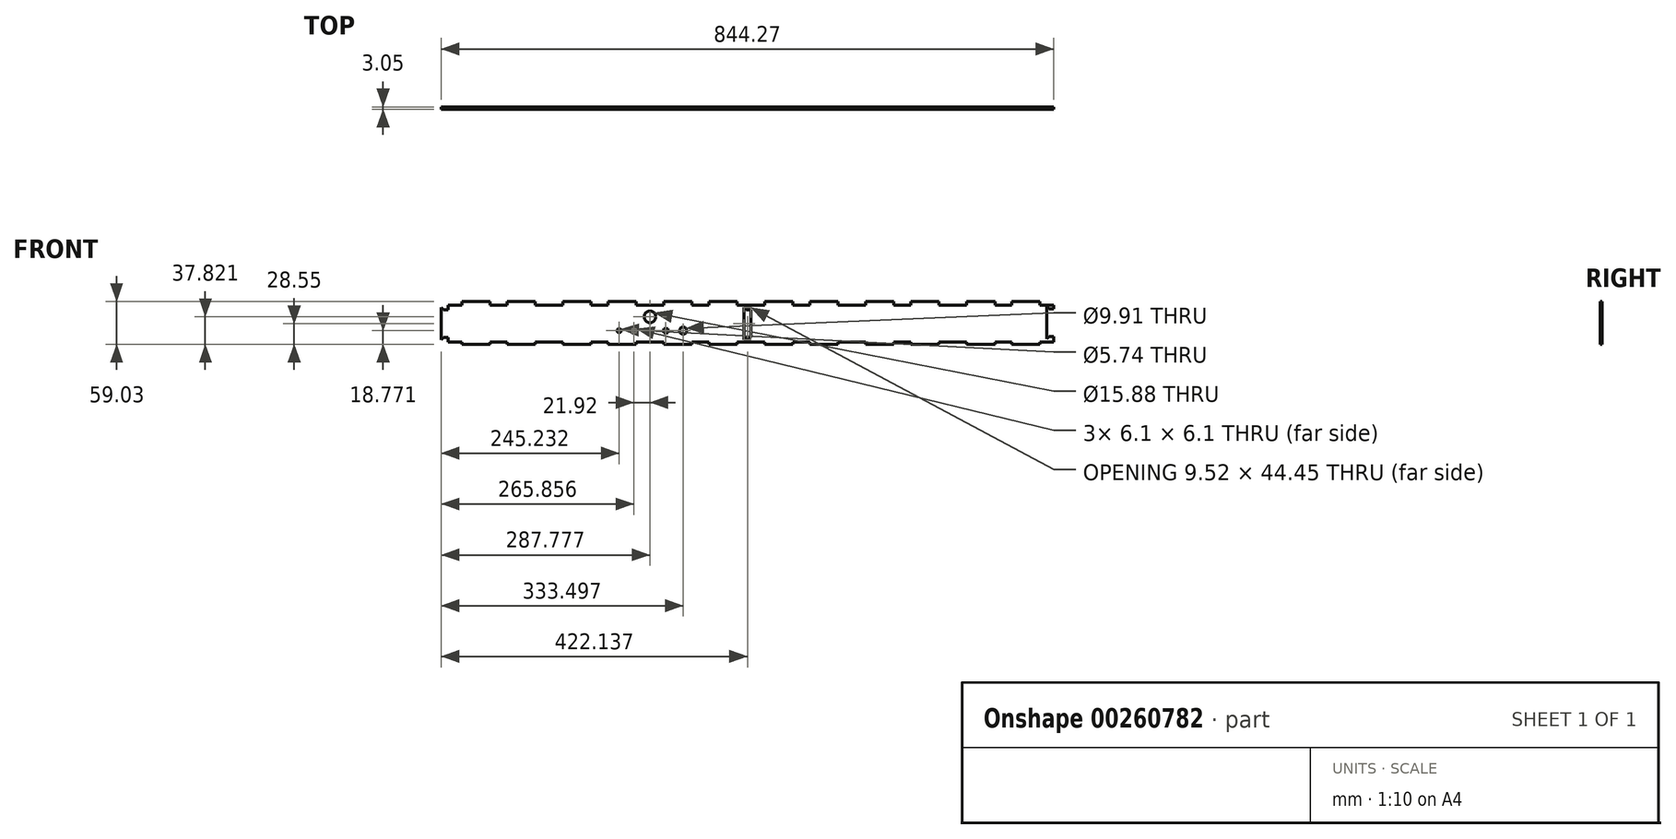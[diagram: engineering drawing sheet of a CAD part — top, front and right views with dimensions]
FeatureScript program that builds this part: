
annotation { "Feature Type Name" : "Feature", "Feature Type Description" : "" }
export const myFeature = defineFeature(function(context is Context, id is Id, definition is map)
    precondition{}
    {
        {
            var Q0;
            Q0=qCreatedBy(makeId("Front.planeOp"),FACE);
            var sketch = newSketch(context, id + "F0", { "sketchPlane" : qUnion([Q0])});
            skLineSegment(sketch, "E0.bottom", {"start": v(0, 0) * mm, "end": v(834.74, 0) * mm});
            skLineSegment(sketch, "E0.top", {"start": v(0, 50.8) * mm, "end": v(834.74, 50.8) * mm});
            skLineSegment(sketch, "E0.left", {"start": v(0, 0) * mm, "end": v(0, 50.8) * mm});
            skLineSegment(sketch, "E0.right", {"start": v(834.74, 0) * mm, "end": v(834.74, 50.8) * mm});
            skLineSegment(sketch, "E1", {"start": v(57.92, 50.8) * mm, "end": v(57.92, 0) * mm, "construction": true});
            skLineSegment(sketch, "E2", {"start": v(75.88, 50.8) * mm, "end": v(75.88, 0) * mm, "construction": true});
            skLineSegment(sketch, "E3", {"start": v(776.82, 50.8) * mm, "end": v(776.82, 0) * mm, "construction": true});
            skLineSegment(sketch, "E4", {"start": v(758.86, 50.8) * mm, "end": v(758.86, 0) * mm, "construction": true});
            skSolve(sketch);
        }
        {
            var Q0;
            Q0=makeQuery(id+"F0.imprint","IMPRINT",FACE,{"disambiguationData":[TD([[makeQuery(id+"F0.imprint","IMPRINT",EDGE,{"derivedFrom":sQuery(id+"F0.wireOp",EDGE,"E0.bottom")}),1.0]])]});
            extrude(context, id + "F1", {"entities" : qUnion([Q0]), "depth" : 3.05 * mm});
        }
        {
            var Q0;
            Q0=makeQuery(id+"F1.opExtrude","CAP_FACE",FACE,{"disambiguationData":[OSD([sQuery(id+"F0.wireOp",EDGE,"E0.bottom"),sQuery(id+"F0.wireOp",EDGE,"E0.top"),sQuery(id+"F0.wireOp",EDGE,"E0.left"),sQuery(id+"F0.wireOp",EDGE,"E0.right")])],"isStart":false});
            var sketch = newSketch(context, id + "F2", { "sketchPlane" : qUnion([Q0])});
            skLineSegment(sketch, "E5", {"start": v(57.92, 0) * mm, "end": v(57.92, 50.8) * mm});
            skLineSegment(sketch, "E6", {"start": v(81.2, 0) * mm, "end": v(81.2, 50.8) * mm});
            skLineSegment(sketch, "E7", {"start": v(776.82, 0) * mm, "end": v(776.82, 50.8) * mm});
            skLineSegment(sketch, "E8", {"start": v(753.54, 0) * mm, "end": v(753.54, 50.8) * mm});
            skLineSegment(sketch, "E9", {"start": v(197.05, 50.8) * mm, "end": v(197.05, 0) * mm});
            skLineSegment(sketch, "E10", {"start": v(220.32, 0) * mm, "end": v(220.32, 50.8) * mm});
            skLineSegment(sketch, "E11", {"start": v(336.17, 50.8) * mm, "end": v(336.17, 0) * mm});
            skLineSegment(sketch, "E12", {"start": v(359.45, 0.94) * mm, "end": v(359.45, 50.8) * mm});
            skLineSegment(sketch, "E13", {"start": v(475.3, 0) * mm, "end": v(475.3, 50.8) * mm});
            skLineSegment(sketch, "E14", {"start": v(498.57, 0) * mm, "end": v(498.57, 50.8) * mm});
            skLineSegment(sketch, "E15", {"start": v(614.42, 50.8) * mm, "end": v(614.42, 0) * mm});
            skLineSegment(sketch, "E16", {"start": v(637.7, 50.8) * mm, "end": v(637.7, 0) * mm});
            skCircle(sketch, "E17", {"center": v(9.53, 25.4) * mm, "radius": 1.27 * mm});
            skPoint(sketch, "E17.centerSnap0", {"position": v(0, 25.4) * mm});
            skCircle(sketch, "E18", {"center": v(825.22, 25.4) * mm, "radius": 1.27 * mm});
            skSolve(sketch);
        }
        {
            var Q0;
            {var subQ0=sQuery(id+"F2.wireOp",EDGE,"E6");Q0=makeQuery(id+"F2.imprint","IMPRINT",FACE,{"disambiguationData":[TD([[makeQuery(id+"F2.imprint","IMPRINT",EDGE,{"derivedFrom":subQ0}),-1.0]])]});}
            var sketch = newSketch(context, id + "F3", { "sketchPlane" : qUnion([Q0])});
            skLineSegment(sketch, "E19", {"start": v(0, 25.4) * mm, "end": v(834.74, 25.4) * mm, "construction": true});
            skLineSegment(sketch, "E20", {"start": v(0, 50.8) * mm, "end": v(0, 55.88) * mm});
            skLineSegment(sketch, "E21", {"start": v(0, 55.88) * mm, "end": v(57.92, 55.88) * mm});
            skLineSegment(sketch, "E22", {"start": v(57.92, 55.88) * mm, "end": v(57.92, 50.8) * mm});
            skLineSegment(sketch, "E23", {"start": v(81.2, 50.8) * mm, "end": v(81.2, 55.88) * mm});
            skLineSegment(sketch, "E24", {"start": v(81.2, 55.88) * mm, "end": v(197.05, 55.88) * mm});
            skLineSegment(sketch, "E25", {"start": v(197.05, 55.88) * mm, "end": v(197.05, 50.8) * mm});
            skLineSegment(sketch, "E26", {"start": v(220.32, 50.8) * mm, "end": v(220.32, 55.88) * mm});
            skLineSegment(sketch, "E27", {"start": v(220.32, 55.88) * mm, "end": v(336.17, 55.88) * mm});
            skLineSegment(sketch, "E28", {"start": v(336.17, 55.88) * mm, "end": v(336.17, 50.8) * mm});
            skLineSegment(sketch, "E29", {"start": v(359.45, 50.8) * mm, "end": v(359.45, 55.88) * mm});
            skLineSegment(sketch, "E30", {"start": v(359.45, 55.88) * mm, "end": v(475.3, 55.88) * mm});
            skLineSegment(sketch, "E31", {"start": v(475.3, 55.88) * mm, "end": v(475.3, 50.8) * mm});
            skLineSegment(sketch, "E32", {"start": v(498.57, 50.8) * mm, "end": v(498.57, 55.88) * mm});
            skLineSegment(sketch, "E33", {"start": v(498.57, 55.88) * mm, "end": v(614.42, 55.88) * mm});
            skLineSegment(sketch, "E34", {"start": v(614.42, 55.88) * mm, "end": v(614.42, 50.8) * mm});
            skLineSegment(sketch, "E35", {"start": v(637.7, 50.8) * mm, "end": v(637.7, 55.88) * mm});
            skLineSegment(sketch, "E36", {"start": v(637.7, 55.88) * mm, "end": v(753.54, 55.88) * mm});
            skLineSegment(sketch, "E37", {"start": v(753.54, 55.88) * mm, "end": v(753.54, 50.8) * mm});
            skLineSegment(sketch, "E38", {"start": v(776.82, 50.8) * mm, "end": v(776.82, 55.88) * mm});
            skLineSegment(sketch, "E39", {"start": v(776.82, 55.88) * mm, "end": v(834.74, 55.88) * mm});
            skLineSegment(sketch, "E40", {"start": v(834.74, 55.88) * mm, "end": v(834.74, 50.8) * mm});
            skLineSegment(sketch, "E41", {"start": v(0, 50.8) * mm, "end": v(834.74, 50.8) * mm});
            skLineSegment(sketch, "E42.bottom", {"start": v(0, 0) * mm, "end": v(57.92, 0) * mm});
            skLineSegment(sketch, "E42.top", {"start": v(0, -3.15) * mm, "end": v(57.92, -3.15) * mm});
            skLineSegment(sketch, "E42.left", {"start": v(0, 0) * mm, "end": v(0, -3.15) * mm});
            skLineSegment(sketch, "E42.right", {"start": v(57.92, 0) * mm, "end": v(57.92, -3.15) * mm});
            skLineSegment(sketch, "E43.bottom", {"start": v(81.2, 0) * mm, "end": v(197.05, 0) * mm});
            skLineSegment(sketch, "E43.top", {"start": v(81.2, -3.15) * mm, "end": v(197.05, -3.15) * mm});
            skLineSegment(sketch, "E43.left", {"start": v(81.2, 0) * mm, "end": v(81.2, -3.15) * mm});
            skLineSegment(sketch, "E43.right", {"start": v(197.05, 0) * mm, "end": v(197.05, -3.15) * mm});
            skLineSegment(sketch, "E44.bottom", {"start": v(220.32, 0) * mm, "end": v(336.17, 0) * mm});
            skLineSegment(sketch, "E44.top", {"start": v(220.32, -3.15) * mm, "end": v(336.17, -3.15) * mm});
            skLineSegment(sketch, "E44.left", {"start": v(220.32, 0) * mm, "end": v(220.32, -3.15) * mm});
            skLineSegment(sketch, "E44.right", {"start": v(336.17, 0) * mm, "end": v(336.17, -3.15) * mm});
            skLineSegment(sketch, "E45.bottom", {"start": v(359.45, 0) * mm, "end": v(475.3, 0) * mm});
            skLineSegment(sketch, "E45.top", {"start": v(359.45, -3.15) * mm, "end": v(475.3, -3.15) * mm});
            skLineSegment(sketch, "E45.left", {"start": v(359.45, 0) * mm, "end": v(359.45, -3.15) * mm});
            skLineSegment(sketch, "E45.right", {"start": v(475.3, 0) * mm, "end": v(475.3, -3.15) * mm});
            skLineSegment(sketch, "E46.bottom", {"start": v(498.57, 0) * mm, "end": v(614.42, 0) * mm});
            skLineSegment(sketch, "E46.top", {"start": v(498.57, -3.15) * mm, "end": v(614.42, -3.15) * mm});
            skLineSegment(sketch, "E46.left", {"start": v(498.57, 0) * mm, "end": v(498.57, -3.15) * mm});
            skLineSegment(sketch, "E46.right", {"start": v(614.42, 0) * mm, "end": v(614.42, -3.15) * mm});
            skLineSegment(sketch, "E47.bottom", {"start": v(637.7, 0) * mm, "end": v(753.54, 0) * mm});
            skLineSegment(sketch, "E47.top", {"start": v(637.7, -3.15) * mm, "end": v(753.54, -3.15) * mm});
            skLineSegment(sketch, "E47.left", {"start": v(637.7, 0) * mm, "end": v(637.7, -3.15) * mm});
            skLineSegment(sketch, "E47.right", {"start": v(753.54, 0) * mm, "end": v(753.54, -3.15) * mm});
            skLineSegment(sketch, "E48.bottom", {"start": v(776.82, 0) * mm, "end": v(834.74, 0) * mm});
            skLineSegment(sketch, "E48.top", {"start": v(776.82, -3.15) * mm, "end": v(834.74, -3.15) * mm});
            skLineSegment(sketch, "E48.left", {"start": v(776.82, 0) * mm, "end": v(776.82, -3.15) * mm});
            skLineSegment(sketch, "E48.right", {"start": v(834.74, 0) * mm, "end": v(834.74, -3.15) * mm});
            skSolve(sketch);
        }
        {
            var Q0;
            {var subQ0=sQuery(id+"F3.wireOp",EDGE,"E20");Q0=makeQuery(id+"F3.imprint","IMPRINT",FACE,{"disambiguationData":[TD([[makeQuery(id+"F3.imprint","IMPRINT",EDGE,{"derivedFrom":subQ0}),-1.0]])]});}
            var Q1;
            {var subQ0=sQuery(id+"F3.wireOp",EDGE,"E23");Q1=makeQuery(id+"F3.imprint","IMPRINT",FACE,{"disambiguationData":[TD([[makeQuery(id+"F3.imprint","IMPRINT",EDGE,{"derivedFrom":subQ0}),-1.0]])]});}
            var Q2;
            {var subQ0=sQuery(id+"F3.wireOp",EDGE,"300d203a-4e24-4113-8f0b-c0bd62af7ee03.MirrorCS");Q2=makeQuery(id+"F3.imprint","IMPRINT",FACE,{"disambiguationData":[TD([[makeQuery(id+"F3.imprint","IMPRINT",EDGE,{"derivedFrom":subQ0}),1.0]])]});}
            var Q3;
            {var subQ0=sQuery(id+"F3.wireOp",EDGE,"300d203a-4e24-4113-8f0b-c0bd62af7ee06.MirrorCS");Q3=makeQuery(id+"F3.imprint","IMPRINT",FACE,{"disambiguationData":[TD([[makeQuery(id+"F3.imprint","IMPRINT",EDGE,{"derivedFrom":subQ0}),1.0]])]});}
            var Q4;
            {var subQ0=sQuery(id+"F3.wireOp",EDGE,"E26");Q4=makeQuery(id+"F3.imprint","IMPRINT",FACE,{"disambiguationData":[TD([[makeQuery(id+"F3.imprint","IMPRINT",EDGE,{"derivedFrom":subQ0}),-1.0]])]});}
            var Q5;
            {var subQ0=sQuery(id+"F3.wireOp",EDGE,"300d203a-4e24-4113-8f0b-c0bd62af7ee09.MirrorCS");Q5=makeQuery(id+"F3.imprint","IMPRINT",FACE,{"disambiguationData":[TD([[makeQuery(id+"F3.imprint","IMPRINT",EDGE,{"derivedFrom":subQ0}),1.0]])]});}
            var Q6;
            {var subQ0=sQuery(id+"F3.wireOp",EDGE,"E29");Q6=makeQuery(id+"F3.imprint","IMPRINT",FACE,{"disambiguationData":[TD([[makeQuery(id+"F3.imprint","IMPRINT",EDGE,{"derivedFrom":subQ0}),-1.0]])]});}
            var Q7;
            {var subQ0=sQuery(id+"F3.wireOp",EDGE,"300d203a-4e24-4113-8f0b-c0bd62af7ee05.MirrorCS");Q7=makeQuery(id+"F3.imprint","IMPRINT",FACE,{"disambiguationData":[TD([[makeQuery(id+"F3.imprint","IMPRINT",EDGE,{"derivedFrom":subQ0}),1.0]])]});}
            var Q8;
            {var subQ0=sQuery(id+"F3.wireOp",EDGE,"E32");Q8=makeQuery(id+"F3.imprint","IMPRINT",FACE,{"disambiguationData":[TD([[makeQuery(id+"F3.imprint","IMPRINT",EDGE,{"derivedFrom":subQ0}),-1.0]])]});}
            var Q9;
            {var subQ0=sQuery(id+"F3.wireOp",EDGE,"300d203a-4e24-4113-8f0b-c0bd62af7ee02.MirrorCS");Q9=makeQuery(id+"F3.imprint","IMPRINT",FACE,{"disambiguationData":[TD([[makeQuery(id+"F3.imprint","IMPRINT",EDGE,{"derivedFrom":subQ0}),1.0]])]});}
            var Q10;
            {var subQ0=sQuery(id+"F3.wireOp",EDGE,"E35");Q10=makeQuery(id+"F3.imprint","IMPRINT",FACE,{"disambiguationData":[TD([[makeQuery(id+"F3.imprint","IMPRINT",EDGE,{"derivedFrom":subQ0}),-1.0]])]});}
            var Q11;
            {var subQ0=sQuery(id+"F3.wireOp",EDGE,"300d203a-4e24-4113-8f0b-c0bd62af7ee00.MirrorCS");Q11=makeQuery(id+"F3.imprint","IMPRINT",FACE,{"disambiguationData":[TD([[makeQuery(id+"F3.imprint","IMPRINT",EDGE,{"derivedFrom":subQ0}),1.0]])]});}
            var Q12;
            {var subQ0=sQuery(id+"F3.wireOp",EDGE,"E38");Q12=makeQuery(id+"F3.imprint","IMPRINT",FACE,{"disambiguationData":[TD([[makeQuery(id+"F3.imprint","IMPRINT",EDGE,{"derivedFrom":subQ0}),-1.0]])]});}
            var Q13;
            {var subQ0=sQuery(id+"F3.wireOp",EDGE,"300d203a-4e24-4113-8f0b-c0bd62af7ee04.MirrorCS");Q13=makeQuery(id+"F3.imprint","IMPRINT",FACE,{"disambiguationData":[TD([[makeQuery(id+"F3.imprint","IMPRINT",EDGE,{"derivedFrom":subQ0}),1.0]])]});}
            var Q14;
            Q14=makeQuery(id+"F3.imprint","IMPRINT",FACE,{"disambiguationData":[TD([[makeQuery(id+"F3.imprint","IMPRINT",EDGE,{"derivedFrom":sQuery(id+"F3.wireOp",EDGE,"E42.bottom")}),-1.0]])]});
            var Q15;
            Q15=makeQuery(id+"F3.imprint","IMPRINT",FACE,{"disambiguationData":[TD([[makeQuery(id+"F3.imprint","IMPRINT",EDGE,{"derivedFrom":sQuery(id+"F3.wireOp",EDGE,"E43.bottom")}),-1.0]])]});
            var Q16;
            Q16=makeQuery(id+"F3.imprint","IMPRINT",FACE,{"disambiguationData":[TD([[makeQuery(id+"F3.imprint","IMPRINT",EDGE,{"derivedFrom":sQuery(id+"F3.wireOp",EDGE,"E44.bottom")}),-1.0]])]});
            var Q17;
            Q17=makeQuery(id+"F3.imprint","IMPRINT",FACE,{"disambiguationData":[TD([[makeQuery(id+"F3.imprint","IMPRINT",EDGE,{"derivedFrom":sQuery(id+"F3.wireOp",EDGE,"E45.bottom")}),-1.0]])]});
            var Q18;
            Q18=makeQuery(id+"F3.imprint","IMPRINT",FACE,{"disambiguationData":[TD([[makeQuery(id+"F3.imprint","IMPRINT",EDGE,{"derivedFrom":sQuery(id+"F3.wireOp",EDGE,"E46.bottom")}),-1.0]])]});
            var Q19;
            Q19=makeQuery(id+"F3.imprint","IMPRINT",FACE,{"disambiguationData":[TD([[makeQuery(id+"F3.imprint","IMPRINT",EDGE,{"derivedFrom":sQuery(id+"F3.wireOp",EDGE,"E47.bottom")}),-1.0]])]});
            var Q20;
            Q20=makeQuery(id+"F3.imprint","IMPRINT",FACE,{"disambiguationData":[TD([[makeQuery(id+"F3.imprint","IMPRINT",EDGE,{"derivedFrom":sQuery(id+"F3.wireOp",EDGE,"E48.bottom")}),-1.0]])]});
            extrude(context, id + "F4", {"entities" : qUnion([Q0, Q1, Q2, Q3, Q4, Q5, Q6, Q7, Q8, Q9, Q10, Q11, Q12, Q13, Q14, Q15, Q16, Q17, Q18, Q19, Q20]), "operationType" : NewBodyOperationType.ADD, "oppositeDirection" : true, "depth" : 3.05 * mm});
        }
        {
            var Q0;
            {var subQ0=sQuery(id+"F2.wireOp",EDGE,"E6");Q0=makeQuery(id+"F2.imprint","IMPRINT",FACE,{"disambiguationData":[TD([[makeQuery(id+"F2.imprint","IMPRINT",EDGE,{"derivedFrom":subQ0}),-1.0]])]});}
            var sketch = newSketch(context, id + "F5", { "sketchPlane" : qUnion([Q0])});
            skLineSegment(sketch, "E49", {"start": v(0, 6.35) * mm, "end": v(0, 44.45) * mm});
            skPoint(sketch, "E50", {"position": v(0, 25.4) * mm});
            skLineSegment(sketch, "E51", {"start": v(0, 44.45) * mm, "end": v(-6.35, 44.45) * mm});
            skLineSegment(sketch, "E52", {"start": v(0, 6.35) * mm, "end": v(-6.35, 6.35) * mm});
            skLineSegment(sketch, "E53", {"start": v(-6.35, 44.45) * mm, "end": v(-9.52, 47.63) * mm});
            skLineSegment(sketch, "E54", {"start": v(-6.35, 6.35) * mm, "end": v(-9.52, 3.18) * mm});
            skLineSegment(sketch, "E55", {"start": v(-9.52, 47.63) * mm, "end": v(-9.52, 3.18) * mm});
            skLineSegment(sketch, "E56", {"start": v(834.74, 7.32) * mm, "end": v(834.74, 45.42) * mm});
            skPoint(sketch, "E57", {"position": v(834.74, 26.37) * mm});
            skLineSegment(sketch, "E58", {"start": v(834.74, 45.42) * mm, "end": v(828.4, 45.42) * mm});
            skLineSegment(sketch, "E59", {"start": v(834.74, 7.32) * mm, "end": v(828.4, 7.32) * mm});
            skLineSegment(sketch, "E60", {"start": v(828.4, 45.42) * mm, "end": v(825.22, 48.6) * mm});
            skLineSegment(sketch, "E61", {"start": v(828.4, 7.32) * mm, "end": v(825.22, 4.14) * mm});
            skLineSegment(sketch, "E62", {"start": v(825.22, 48.6) * mm, "end": v(825.22, 4.14) * mm});
            skSolve(sketch);
        }
        {
            var Q0;
            Q0=makeQuery(id+"F5.imprint","IMPRINT",FACE,{"disambiguationData":[TD([[makeQuery(id+"F5.imprint","IMPRINT",EDGE,{"derivedFrom":sQuery(id+"F5.wireOp",EDGE,"E49")}),1.0]])]});
            extrude(context, id + "F6", {"entities" : qUnion([Q0]), "operationType" : NewBodyOperationType.ADD, "oppositeDirection" : true, "depth" : 3.05 * mm});
        }
        {
            var Q0;
            Q0=makeQuery(id+"F5.imprint","IMPRINT",FACE,{"disambiguationData":[TD([[makeQuery(id+"F5.imprint","IMPRINT",EDGE,{"derivedFrom":sQuery(id+"F5.wireOp",EDGE,"E56")}),1.0]])]});
            extrude(context, id + "F7", {"entities" : qUnion([Q0]), "operationType" : NewBodyOperationType.REMOVE, "endBound" : BoundingType.THROUGH_ALL, "oppositeDirection" : true, "depth" : 25.4 * mm});
        }
        {
            var Q0;
            {var subQ0=sQuery(id+"F2.wireOp",EDGE,"E11");Q0=makeQuery(id+"F2.imprint","IMPRINT",FACE,{"disambiguationData":[TD([[makeQuery(id+"F2.imprint","IMPRINT",EDGE,{"derivedFrom":subQ0}),1.0]])]});}
            var sketch = newSketch(context, id + "F8", { "sketchPlane" : qUnion([Q0])});
            skLineSegment(sketch, "E63", {"start": v(417.37, 6.35) * mm, "end": v(417.37, 44.45) * mm});
            skLineSegment(sketch, "E64", {"start": v(417.37, 44.45) * mm, "end": v(411.02, 44.45) * mm});
            skLineSegment(sketch, "E65", {"start": v(411.02, 44.45) * mm, "end": v(407.85, 47.63) * mm});
            skLineSegment(sketch, "E66", {"start": v(407.85, 47.63) * mm, "end": v(407.85, 3.18) * mm});
            skLineSegment(sketch, "E67", {"start": v(407.85, 3.17) * mm, "end": v(411.02, 6.35) * mm});
            skLineSegment(sketch, "E68", {"start": v(411.02, 6.35) * mm, "end": v(417.37, 6.35) * mm});
            skPoint(sketch, "E69", {"position": v(417.37, 25.4) * mm});
            skPoint(sketch, "E70", {"position": v(407.85, 25.4) * mm});
            skLineSegment(sketch, "E71", {"start": v(407.85, 25.4) * mm, "end": v(417.37, 25.4) * mm, "construction": true});
            skSolve(sketch);
        }
        {
            var Q0;
            {var subQ0=sQuery(id+"F2.wireOp",EDGE,"E10");Q0=makeQuery(id+"F2.imprint","IMPRINT",FACE,{"disambiguationData":[TD([[makeQuery(id+"F2.imprint","IMPRINT",EDGE,{"derivedFrom":subQ0}),-1.0]])]});}
            var sketch = newSketch(context, id + "F9", { "sketchPlane" : qUnion([Q0])});
            skLineSegment(sketch, "E72.bottom", {"start": v(245.23, 21.59) * mm, "end": v(311.27, 21.59) * mm, "construction": true});
            skLineSegment(sketch, "E72.top", {"start": v(245.23, 9.65) * mm, "end": v(311.27, 9.65) * mm, "construction": true});
            skLineSegment(sketch, "E72.left", {"start": v(245.23, 21.59) * mm, "end": v(245.23, 9.65) * mm, "construction": true});
            skLineSegment(sketch, "E72.right", {"start": v(311.27, 21.59) * mm, "end": v(311.27, 9.65) * mm, "construction": true});
            skPoint(sketch, "E73", {"position": v(278.25, 9.65) * mm});
            skLineSegment(sketch, "E74.bottom", {"start": v(253.28, 12.57) * mm, "end": v(259.37, 12.57) * mm});
            skLineSegment(sketch, "E74.top", {"start": v(253.28, 18.67) * mm, "end": v(259.37, 18.67) * mm});
            skLineSegment(sketch, "E74.left", {"start": v(253.28, 12.57) * mm, "end": v(253.28, 18.67) * mm});
            skLineSegment(sketch, "E74.right", {"start": v(259.37, 12.57) * mm, "end": v(259.37, 18.67) * mm});
            skLineSegment(sketch, "E75.bottom", {"start": v(275.2, 12.57) * mm, "end": v(281.3, 12.57) * mm});
            skLineSegment(sketch, "E75.top", {"start": v(275.2, 18.67) * mm, "end": v(281.3, 18.67) * mm});
            skLineSegment(sketch, "E75.left", {"start": v(275.2, 12.57) * mm, "end": v(275.2, 18.67) * mm});
            skLineSegment(sketch, "E75.right", {"start": v(281.3, 12.57) * mm, "end": v(281.3, 18.67) * mm});
            skLineSegment(sketch, "E76.bottom", {"start": v(297.12, 12.57) * mm, "end": v(303.21, 12.57) * mm});
            skLineSegment(sketch, "E76.top", {"start": v(297.12, 18.67) * mm, "end": v(303.21, 18.67) * mm});
            skLineSegment(sketch, "E76.left", {"start": v(297.12, 12.57) * mm, "end": v(297.12, 18.67) * mm});
            skLineSegment(sketch, "E76.right", {"start": v(303.21, 12.57) * mm, "end": v(303.21, 18.67) * mm});
            skPoint(sketch, "E77", {"position": v(253.28, 15.62) * mm});
            skPoint(sketch, "E78", {"position": v(245.23, 15.62) * mm});
            skPoint(sketch, "E79", {"position": v(278.25, 18.67) * mm});
            skPoint(sketch, "E80", {"position": v(275.2, 15.62) * mm});
            skPoint(sketch, "E81", {"position": v(297.12, 15.62) * mm});
            skPoint(sketch, "E82", {"position": v(300.17, 18.67) * mm});
            skCircle(sketch, "E83", {"center": v(235.7, 15.62) * mm, "radius": 2.87 * mm});
            skCircle(sketch, "E84", {"center": v(323.97, 15.62) * mm, "radius": 4.95 * mm});
            skCircle(sketch, "E85", {"center": v(278.25, 34.67) * mm, "radius": 7.94 * mm});
            skSolve(sketch);
        }
        {
            var Q0;
            Q0=qSketchRegion(id+"F9",true);
            extrude(context, id + "F10", {"entities" : qUnion([Q0]), "operationType" : NewBodyOperationType.REMOVE, "endBound" : BoundingType.THROUGH_ALL, "oppositeDirection" : true, "depth" : 25.4 * mm});
        }
        {
            var Q0;
            Q0=qSketchRegion(id+"F8",true);
            extrude(context, id + "F11", {"entities" : qUnion([Q0]), "operationType" : NewBodyOperationType.REMOVE, "oppositeDirection" : true, "depth" : 25.4 * mm});
        }
        {
            var Q0;
            {var subQ0=sQuery(id+"F2.wireOp",EDGE,"E6");Q0=makeQuery(id+"F2.imprint","IMPRINT",FACE,{"disambiguationData":[TD([[makeQuery(id+"F2.imprint","IMPRINT",EDGE,{"derivedFrom":subQ0}),-1.0]])]});}
            var sketch = newSketch(context, id + "F12", { "sketchPlane" : qUnion([Q0])});
            skLineSegment(sketch, "E86.bottom", {"start": v(120.07, 55.88) * mm, "end": v(158.17, 55.88) * mm});
            skLineSegment(sketch, "E86.top", {"start": v(120.07, 50.8) * mm, "end": v(158.17, 50.8) * mm});
            skLineSegment(sketch, "E86.left", {"start": v(120.07, 55.88) * mm, "end": v(120.07, 50.8) * mm});
            skLineSegment(sketch, "E86.right", {"start": v(158.17, 55.88) * mm, "end": v(158.17, 50.8) * mm});
            skLineSegment(sketch, "E87.bottom", {"start": v(259.2, 55.88) * mm, "end": v(297.3, 55.88) * mm});
            skLineSegment(sketch, "E87.top", {"start": v(259.2, 50.8) * mm, "end": v(297.3, 50.8) * mm});
            skLineSegment(sketch, "E87.left", {"start": v(259.2, 55.88) * mm, "end": v(259.2, 50.8) * mm});
            skLineSegment(sketch, "E87.right", {"start": v(297.3, 55.88) * mm, "end": v(297.3, 50.8) * mm});
            skLineSegment(sketch, "E88.bottom", {"start": v(398.32, 55.88) * mm, "end": v(436.42, 55.88) * mm});
            skLineSegment(sketch, "E88.top", {"start": v(398.32, 50.8) * mm, "end": v(436.42, 50.8) * mm});
            skLineSegment(sketch, "E88.left", {"start": v(398.32, 55.88) * mm, "end": v(398.32, 50.8) * mm});
            skLineSegment(sketch, "E88.right", {"start": v(436.42, 55.88) * mm, "end": v(436.42, 50.8) * mm});
            skLineSegment(sketch, "E89.bottom", {"start": v(537.44, 55.88) * mm, "end": v(575.54, 55.88) * mm});
            skLineSegment(sketch, "E89.top", {"start": v(537.44, 50.8) * mm, "end": v(575.54, 50.8) * mm});
            skLineSegment(sketch, "E89.left", {"start": v(537.44, 55.88) * mm, "end": v(537.44, 50.8) * mm});
            skLineSegment(sketch, "E89.right", {"start": v(575.54, 55.88) * mm, "end": v(575.54, 50.8) * mm});
            skLineSegment(sketch, "E90.bottom", {"start": v(676.57, 55.88) * mm, "end": v(714.67, 55.88) * mm});
            skLineSegment(sketch, "E90.top", {"start": v(676.57, 50.8) * mm, "end": v(714.67, 50.8) * mm});
            skLineSegment(sketch, "E90.left", {"start": v(676.57, 55.88) * mm, "end": v(676.57, 50.8) * mm});
            skLineSegment(sketch, "E90.right", {"start": v(714.67, 55.88) * mm, "end": v(714.67, 50.8) * mm});
            skLineSegment(sketch, "E91.bottom", {"start": v(815.7, 55.88) * mm, "end": v(853.8, 55.88) * mm});
            skLineSegment(sketch, "E91.top", {"start": v(815.7, 50.8) * mm, "end": v(853.8, 50.8) * mm});
            skLineSegment(sketch, "E91.left", {"start": v(815.7, 55.88) * mm, "end": v(815.7, 50.8) * mm});
            skLineSegment(sketch, "E91.right", {"start": v(853.8, 55.88) * mm, "end": v(853.8, 50.8) * mm});
            skLineSegment(sketch, "E92.bottom", {"start": v(19.05, 50.8) * mm, "end": v(-19.05, 50.8) * mm});
            skLineSegment(sketch, "E92.top", {"start": v(19.05, 55.88) * mm, "end": v(-19.05, 55.88) * mm});
            skLineSegment(sketch, "E92.left", {"start": v(19.05, 50.8) * mm, "end": v(19.05, 55.88) * mm});
            skLineSegment(sketch, "E92.right", {"start": v(-19.05, 50.8) * mm, "end": v(-19.05, 55.88) * mm});
            skLineSegment(sketch, "E93.bottom", {"start": v(19.05, -3.15) * mm, "end": v(-19.05, -3.15) * mm});
            skLineSegment(sketch, "E93.top", {"start": v(19.05, 0) * mm, "end": v(-19.05, 0) * mm});
            skLineSegment(sketch, "E93.left", {"start": v(19.05, -3.15) * mm, "end": v(19.05, 0) * mm});
            skLineSegment(sketch, "E93.right", {"start": v(-19.05, -3.15) * mm, "end": v(-19.05, 0) * mm});
            skLineSegment(sketch, "E94.bottom", {"start": v(158.17, -3.15) * mm, "end": v(120.07, -3.15) * mm});
            skLineSegment(sketch, "E94.top", {"start": v(158.17, 0) * mm, "end": v(120.07, 0) * mm});
            skLineSegment(sketch, "E94.left", {"start": v(158.17, -3.15) * mm, "end": v(158.17, 0) * mm});
            skLineSegment(sketch, "E94.right", {"start": v(120.07, -3.15) * mm, "end": v(120.07, 0) * mm});
            skLineSegment(sketch, "E95.bottom", {"start": v(297.3, -3.15) * mm, "end": v(259.2, -3.15) * mm});
            skLineSegment(sketch, "E95.top", {"start": v(297.3, 0) * mm, "end": v(259.2, 0) * mm});
            skLineSegment(sketch, "E95.left", {"start": v(297.3, -3.15) * mm, "end": v(297.3, 0) * mm});
            skLineSegment(sketch, "E95.right", {"start": v(259.2, -3.15) * mm, "end": v(259.2, 0) * mm});
            skLineSegment(sketch, "E96.bottom", {"start": v(436.42, -3.15) * mm, "end": v(398.32, -3.15) * mm});
            skLineSegment(sketch, "E96.top", {"start": v(436.42, 0) * mm, "end": v(398.32, 0) * mm});
            skLineSegment(sketch, "E96.left", {"start": v(436.42, -3.15) * mm, "end": v(436.42, 0) * mm});
            skLineSegment(sketch, "E96.right", {"start": v(398.32, -3.15) * mm, "end": v(398.32, 0) * mm});
            skLineSegment(sketch, "E97.bottom", {"start": v(575.54, -3.15) * mm, "end": v(537.44, -3.15) * mm});
            skLineSegment(sketch, "E97.top", {"start": v(575.54, 0) * mm, "end": v(537.44, 0) * mm});
            skLineSegment(sketch, "E97.left", {"start": v(575.54, -3.15) * mm, "end": v(575.54, 0) * mm});
            skLineSegment(sketch, "E97.right", {"start": v(537.44, -3.15) * mm, "end": v(537.44, 0) * mm});
            skLineSegment(sketch, "E98.bottom", {"start": v(714.67, -3.15) * mm, "end": v(676.57, -3.15) * mm});
            skLineSegment(sketch, "E98.top", {"start": v(714.67, 0) * mm, "end": v(676.57, 0) * mm});
            skLineSegment(sketch, "E98.left", {"start": v(714.67, -3.15) * mm, "end": v(714.67, 0) * mm});
            skLineSegment(sketch, "E98.right", {"start": v(676.57, -3.15) * mm, "end": v(676.57, 0) * mm});
            skLineSegment(sketch, "E99.bottom", {"start": v(853.8, -3.15) * mm, "end": v(815.7, -3.15) * mm});
            skLineSegment(sketch, "E99.top", {"start": v(853.8, 0) * mm, "end": v(815.7, 0) * mm});
            skLineSegment(sketch, "E99.left", {"start": v(853.8, -3.15) * mm, "end": v(853.8, 0) * mm});
            skLineSegment(sketch, "E99.right", {"start": v(815.7, -3.15) * mm, "end": v(815.7, 0) * mm});
            skPoint(sketch, "E100", {"position": v(0, 55.88) * mm});
            skPoint(sketch, "E101", {"position": v(139.12, 55.88) * mm});
            skPoint(sketch, "E102", {"position": v(278.25, 55.88) * mm});
            skPoint(sketch, "E103", {"position": v(417.37, 55.88) * mm});
            skPoint(sketch, "E104", {"position": v(556.5, 55.88) * mm});
            skPoint(sketch, "E105", {"position": v(695.62, 55.88) * mm});
            skPoint(sketch, "E106", {"position": v(834.74, 55.88) * mm});
            skPoint(sketch, "E107", {"position": v(834.74, -3.15) * mm});
            skPoint(sketch, "E108", {"position": v(695.62, -3.15) * mm});
            skPoint(sketch, "E109", {"position": v(556.5, -3.15) * mm});
            skPoint(sketch, "E110", {"position": v(417.37, -3.15) * mm});
            skPoint(sketch, "E111", {"position": v(278.25, -3.15) * mm});
            skPoint(sketch, "E112", {"position": v(139.12, -3.15) * mm});
            skPoint(sketch, "E113", {"position": v(0, -3.15) * mm});
            skSolve(sketch);
        }
        {
            var Q0;
            Q0 = qSketchRegion(id + "F12", true);
            var Q1;
            {var subQ0=sQuery(id+"F3.wireOp",EDGE,"E41");Q1=makeQuery(id+"F6.boolean.opBoolean","MERGE",FACE,{"derivedFrom":[makeQuery(id+"F4.boolean.opBoolean","MERGE",FACE,{"derivedFrom":[makeQuery(id+"F1.opExtrude","CAP_FACE",FACE,{"disambiguationData":[OSD([sQuery(id+"F0.wireOp",EDGE,"E0.bottom"),sQuery(id+"F0.wireOp",EDGE,"E0.top"),sQuery(id+"F0.wireOp",EDGE,"E0.left"),sQuery(id+"F0.wireOp",EDGE,"E0.right")])],"isStart":true}),makeQuery(id+"F4.opExtrude","CAP_FACE",FACE,{"disambiguationData":[OSD([sQuery(id+"F3.wireOp",EDGE,"E20"),sQuery(id+"F3.wireOp",EDGE,"E21"),sQuery(id+"F3.wireOp",EDGE,"E22"),subQ0])],"isStart":false}),makeQuery(id+"F4.opExtrude","CAP_FACE",FACE,{"disambiguationData":[OSD([sQuery(id+"F3.wireOp",EDGE,"E23"),sQuery(id+"F3.wireOp",EDGE,"E24"),sQuery(id+"F3.wireOp",EDGE,"E25"),subQ0])],"isStart":false}),makeQuery(id+"F4.opExtrude","CAP_FACE",FACE,{"disambiguationData":[OSD([sQuery(id+"F3.wireOp",EDGE,"E26"),sQuery(id+"F3.wireOp",EDGE,"E27"),sQuery(id+"F3.wireOp",EDGE,"E28"),subQ0])],"isStart":false}),makeQuery(id+"F4.opExtrude","CAP_FACE",FACE,{"disambiguationData":[OSD([sQuery(id+"F3.wireOp",EDGE,"E29"),sQuery(id+"F3.wireOp",EDGE,"E30"),sQuery(id+"F3.wireOp",EDGE,"E31"),subQ0])],"isStart":false}),makeQuery(id+"F4.opExtrude","CAP_FACE",FACE,{"disambiguationData":[OSD([sQuery(id+"F3.wireOp",EDGE,"E32"),sQuery(id+"F3.wireOp",EDGE,"E33"),sQuery(id+"F3.wireOp",EDGE,"E34"),subQ0])],"isStart":false}),makeQuery(id+"F4.opExtrude","CAP_FACE",FACE,{"disambiguationData":[OSD([sQuery(id+"F3.wireOp",EDGE,"E35"),sQuery(id+"F3.wireOp",EDGE,"E36"),sQuery(id+"F3.wireOp",EDGE,"E37"),subQ0])],"isStart":false}),makeQuery(id+"F4.opExtrude","CAP_FACE",FACE,{"disambiguationData":[OSD([sQuery(id+"F3.wireOp",EDGE,"E38"),sQuery(id+"F3.wireOp",EDGE,"E39"),sQuery(id+"F3.wireOp",EDGE,"E40"),subQ0])],"isStart":false}),makeQuery(id+"F4.opExtrude","CAP_FACE",FACE,{"disambiguationData":[OSD([sQuery(id+"F3.wireOp",EDGE,"E42.bottom"),sQuery(id+"F3.wireOp",EDGE,"E42.top"),sQuery(id+"F3.wireOp",EDGE,"E42.left"),sQuery(id+"F3.wireOp",EDGE,"E42.right")])],"isStart":false}),makeQuery(id+"F4.opExtrude","CAP_FACE",FACE,{"disambiguationData":[OSD([sQuery(id+"F3.wireOp",EDGE,"E43.bottom"),sQuery(id+"F3.wireOp",EDGE,"E43.top"),sQuery(id+"F3.wireOp",EDGE,"E43.left"),sQuery(id+"F3.wireOp",EDGE,"E43.right")])],"isStart":false}),makeQuery(id+"F4.opExtrude","CAP_FACE",FACE,{"disambiguationData":[OSD([sQuery(id+"F3.wireOp",EDGE,"E44.bottom"),sQuery(id+"F3.wireOp",EDGE,"E44.top"),sQuery(id+"F3.wireOp",EDGE,"E44.left"),sQuery(id+"F3.wireOp",EDGE,"E44.right")])],"isStart":false}),makeQuery(id+"F4.opExtrude","CAP_FACE",FACE,{"disambiguationData":[OSD([sQuery(id+"F3.wireOp",EDGE,"E45.bottom"),sQuery(id+"F3.wireOp",EDGE,"E45.top"),sQuery(id+"F3.wireOp",EDGE,"E45.left"),sQuery(id+"F3.wireOp",EDGE,"E45.right")])],"isStart":false}),makeQuery(id+"F4.opExtrude","CAP_FACE",FACE,{"disambiguationData":[OSD([sQuery(id+"F3.wireOp",EDGE,"E46.bottom"),sQuery(id+"F3.wireOp",EDGE,"E46.top"),sQuery(id+"F3.wireOp",EDGE,"E46.left"),sQuery(id+"F3.wireOp",EDGE,"E46.right")])],"isStart":false}),makeQuery(id+"F4.opExtrude","CAP_FACE",FACE,{"disambiguationData":[OSD([sQuery(id+"F3.wireOp",EDGE,"E47.bottom"),sQuery(id+"F3.wireOp",EDGE,"E47.top"),sQuery(id+"F3.wireOp",EDGE,"E47.left"),sQuery(id+"F3.wireOp",EDGE,"E47.right")])],"isStart":false}),makeQuery(id+"F4.opExtrude","CAP_FACE",FACE,{"disambiguationData":[OSD([sQuery(id+"F3.wireOp",EDGE,"E48.bottom"),sQuery(id+"F3.wireOp",EDGE,"E48.top"),sQuery(id+"F3.wireOp",EDGE,"E48.left"),sQuery(id+"F3.wireOp",EDGE,"E48.right")])],"isStart":false})]}),makeQuery(id+"F6.opExtrude","CAP_FACE",FACE,{"disambiguationData":[OSD([sQuery(id+"F5.wireOp",EDGE,"E49"),sQuery(id+"F5.wireOp",EDGE,"E51"),sQuery(id+"F5.wireOp",EDGE,"E52"),sQuery(id+"F5.wireOp",EDGE,"E53"),sQuery(id+"F5.wireOp",EDGE,"E54"),sQuery(id+"F5.wireOp",EDGE,"E55")])],"isStart":false})]});}
            extrude(context, id + "F13", {"entities" : qUnion([Q0]), "operationType" : NewBodyOperationType.REMOVE, "endBound" : BoundingType.UP_TO_SURFACE, "oppositeDirection" : true, "endBoundEntityFace" : qUnion([Q1]), "depth" : 25.4 * mm});
        }
    });
